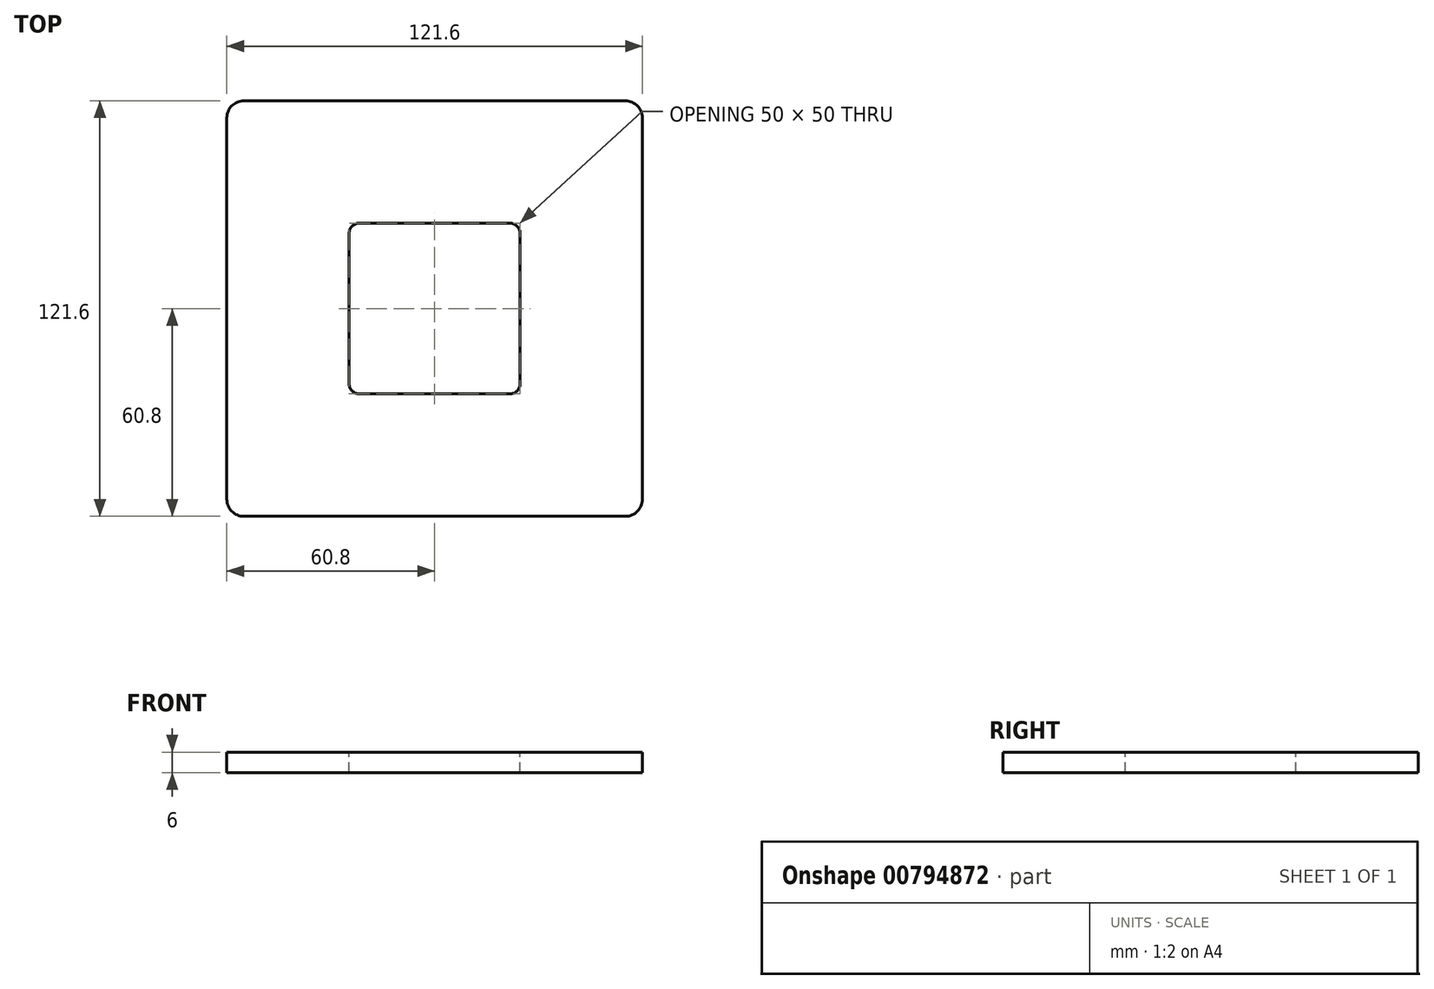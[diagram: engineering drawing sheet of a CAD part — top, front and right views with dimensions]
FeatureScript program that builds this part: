
annotation { "Feature Type Name" : "Feature", "Feature Type Description" : "" }
export const myFeature = defineFeature(function(context is Context, id is Id, definition is map)
    precondition{}
    {
        {
            var Q0;
            Q0=qCreatedBy(makeId("Top.planeOp"),FACE);
            var sketch = newSketch(context, id + "F0", { "sketchPlane" : qUnion([Q0])});
            skLineSegment(sketch, "E0.bottom", {"start": v(55.8, -60.8) * mm, "end": v(-55.8, -60.8) * mm});
            skLineSegment(sketch, "E0.top", {"start": v(55.8, 60.8) * mm, "end": v(-55.8, 60.8) * mm});
            skLineSegment(sketch, "E0.left", {"start": v(60.8, -55.8) * mm, "end": v(60.8, 55.8) * mm});
            skLineSegment(sketch, "E0.right", {"start": v(-60.8, -55.8) * mm, "end": v(-60.8, 55.8) * mm});
            skPoint(sketch, "E0.middle", {"position": v(0, 0) * mm});
            skPoint(sketch, "E1.visualSharp", {"position": v(-60.8, 60.8) * mm});
            skArc(sketch, "E1.filletArc", {"start": v(-55.8, 60.8) * mm, "mid": v(-59.34, 59.34) * mm, "end": v(-60.8, 55.8) * mm});
            skPoint(sketch, "E2.visualSharp", {"position": v(60.8, 60.8) * mm});
            skArc(sketch, "E2.filletArc", {"start": v(60.8, 55.8) * mm, "mid": v(59.34, 59.34) * mm, "end": v(55.8, 60.8) * mm});
            skPoint(sketch, "E3.visualSharp", {"position": v(60.8, -60.8) * mm});
            skArc(sketch, "E3.filletArc", {"start": v(55.8, -60.8) * mm, "mid": v(59.34, -59.34) * mm, "end": v(60.8, -55.8) * mm});
            skPoint(sketch, "E4.visualSharp", {"position": v(-60.8, -60.8) * mm});
            skArc(sketch, "E4.filletArc", {"start": v(-60.8, -55.8) * mm, "mid": v(-59.34, -59.34) * mm, "end": v(-55.8, -60.8) * mm});
            skSolve(sketch);
        }
        {
            var Q0;
            Q0 = qSketchRegion(id + "F0", true);
            extrude(context, id + "F1", {"entities" : qUnion([Q0]), "oppositeDirection" : true, "depth" : 6 * mm, "offsetDistance" : 25 * mm});
        }
        {
            var Q0;
            Q0=makeQuery(id+"F1.opExtrude","CAP_FACE",FACE,{"disambiguationData":[OSD([sQuery(id+"F0.wireOp",EDGE,"E0.bottom"),sQuery(id+"F0.wireOp",EDGE,"E0.top"),sQuery(id+"F0.wireOp",EDGE,"E0.left"),sQuery(id+"F0.wireOp",EDGE,"E0.right"),sQuery(id+"F0.wireOp",EDGE,"E1.filletArc"),sQuery(id+"F0.wireOp",EDGE,"E2.filletArc"),sQuery(id+"F0.wireOp",EDGE,"E3.filletArc"),sQuery(id+"F0.wireOp",EDGE,"E4.filletArc")])],"isStart":true});
            var sketch = newSketch(context, id + "F2", { "sketchPlane" : qUnion([Q0])});
            skLineSegment(sketch, "E5.bottom", {"start": v(22, -25) * mm, "end": v(-22, -25) * mm});
            skLineSegment(sketch, "E5.top", {"start": v(22, 25) * mm, "end": v(-22, 25) * mm});
            skLineSegment(sketch, "E5.left", {"start": v(25, -22) * mm, "end": v(25, 22) * mm});
            skLineSegment(sketch, "E5.right", {"start": v(-25, -22) * mm, "end": v(-25, 22) * mm});
            skPoint(sketch, "E5.middle", {"position": v(0, 0) * mm});
            skPoint(sketch, "E6.visualSharp", {"position": v(-25, 25) * mm});
            skArc(sketch, "E6.filletArc", {"start": v(-22, 25) * mm, "mid": v(-24.12, 24.12) * mm, "end": v(-25, 22) * mm});
            skPoint(sketch, "E7.visualSharp", {"position": v(25, 25) * mm});
            skArc(sketch, "E7.filletArc", {"start": v(25, 22) * mm, "mid": v(24.12, 24.12) * mm, "end": v(22, 25) * mm});
            skPoint(sketch, "E8.visualSharp", {"position": v(25, -25) * mm});
            skArc(sketch, "E8.filletArc", {"start": v(22, -25) * mm, "mid": v(24.12, -24.12) * mm, "end": v(25, -22) * mm});
            skPoint(sketch, "E9.visualSharp", {"position": v(-25, -25) * mm});
            skArc(sketch, "E9.filletArc", {"start": v(-25, -22) * mm, "mid": v(-24.12, -24.12) * mm, "end": v(-22, -25) * mm});
            skSolve(sketch);
        }
        {
            var Q0;
            Q0 = qSketchRegion(id + "F2", true);
            extrude(context, id + "F3", {"entities" : qUnion([Q0]), "operationType" : NewBodyOperationType.REMOVE, "oppositeDirection" : true, "depth" : 10 * mm, "offsetDistance" : 25 * mm});
        }
    });
